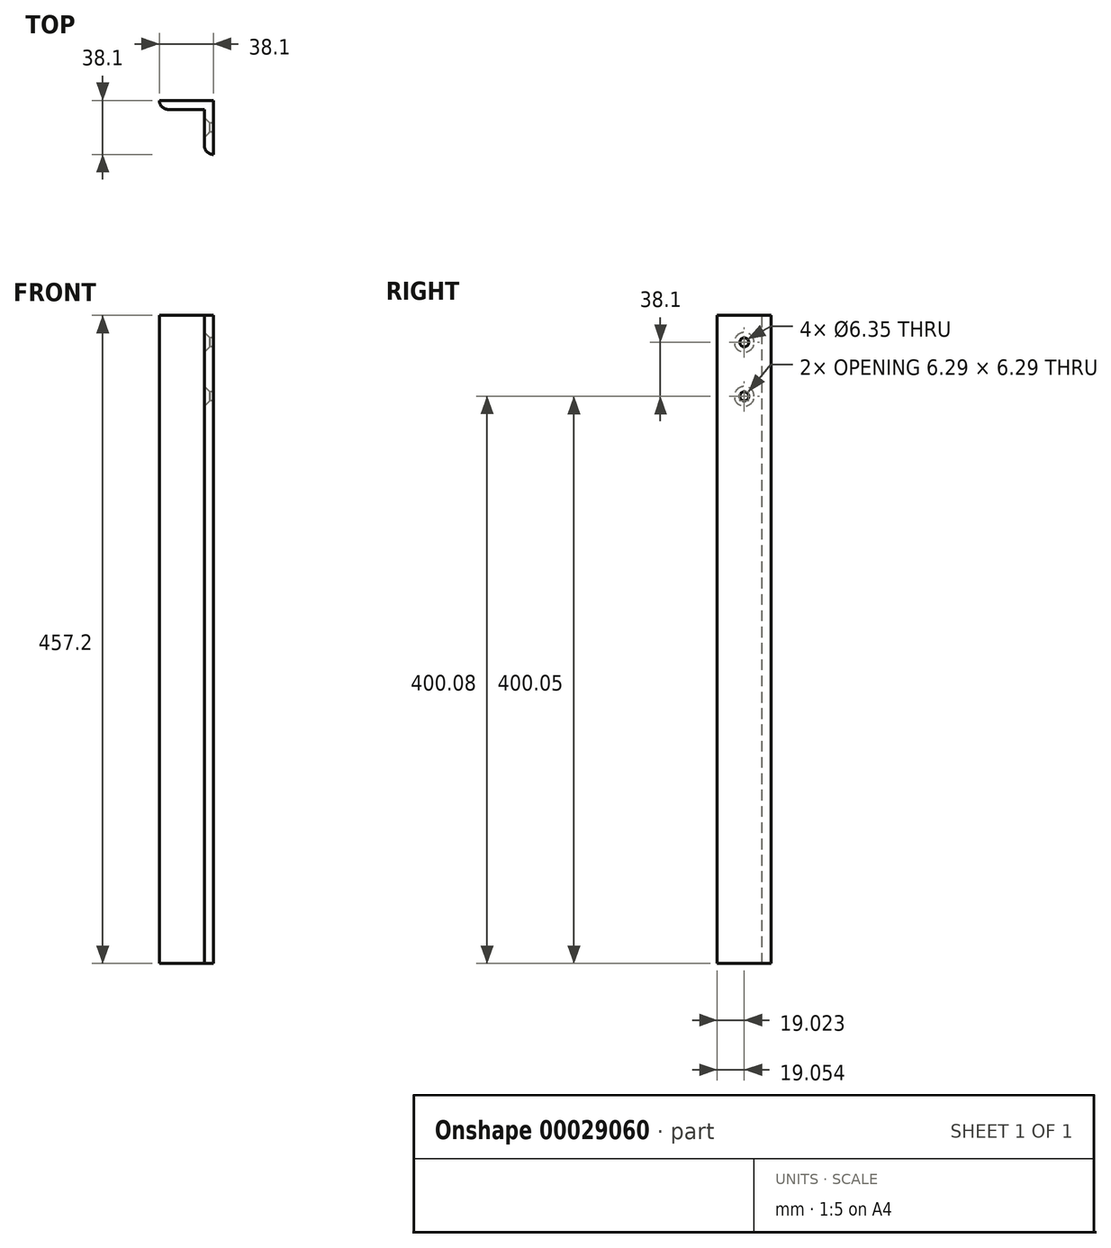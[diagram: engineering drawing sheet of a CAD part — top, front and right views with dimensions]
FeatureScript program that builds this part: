
annotation { "Feature Type Name" : "Feature", "Feature Type Description" : "" }
export const myFeature = defineFeature(function(context is Context, id is Id, definition is map)
    precondition{}
    {
        {
            var Q0;
            Q0=qCreatedBy(makeId("Top.planeOp"),FACE);
            var sketch = newSketch(context, id + "F0", { "sketchPlane" : qUnion([Q0])});
            skLineSegment(sketch, "E0.bottom", {"start": v(-21.42, 16.68) * mm, "end": v(16.68, 16.68) * mm});
            skLineSegment(sketch, "E0.top", {"start": v(-15.07, 10.33) * mm, "end": v(10.33, 10.33) * mm});
            skLineSegment(sketch, "E0.left", {"start": v(-21.42, 16.68) * mm, "end": v(-21.42, 16.68) * mm});
            skLineSegment(sketch, "E1.top", {"start": v(16.68, -21.42) * mm, "end": v(16.68, -21.42) * mm});
            skLineSegment(sketch, "E1.left", {"start": v(16.68, 16.68) * mm, "end": v(16.68, -21.42) * mm});
            skLineSegment(sketch, "E1.right", {"start": v(10.33, 10.33) * mm, "end": v(10.33, -15.07) * mm});
            skPoint(sketch, "E2.visualSharp", {"position": v(-21.42, 10.33) * mm});
            skArc(sketch, "E2.filletArc", {"start": v(-21.42, 16.68) * mm, "mid": v(-19.56, 12.2) * mm, "end": v(-15.07, 10.33) * mm});
            skPoint(sketch, "E3.visualSharp", {"position": v(10.33, -21.42) * mm});
            skArc(sketch, "E3.filletArc", {"start": v(10.33, -15.07) * mm, "mid": v(12.2, -19.56) * mm, "end": v(16.68, -21.42) * mm});
            skSolve(sketch);
        }
        {
            var Q0;
            Q0=makeQuery(id+"F0.imprint","IMPRINT",FACE,{"disambiguationData":[TD([[makeQuery(id+"F0.imprint","IMPRINT",EDGE,{"derivedFrom":sQuery(id+"F0.wireOp",EDGE,"E0.bottom")}),-1.0]])]});
            extrude(context, id + "F1", {"entities" : qUnion([Q0]), "oppositeDirection" : true, "depth" : 457.2 * mm});
        }
        {
            var Q0;
            Q0=makeQuery(id+"F1.opExtrude","SWEPT_FACE",FACE,{"disambiguationData":[OSD([sQuery(id+"F0.wireOp",EDGE,"E1.right")])]});
            var sketch = newSketch(context, id + "F2", { "sketchPlane" : qUnion([Q0])});
            skPoint(sketch, "E4", {"position": v(2.37, -19.05) * mm});
            skPoint(sketch, "E5", {"position": v(2.37, -57.15) * mm});
            skSolve(sketch);
        }
        {
            var Q0;
            Q0=sQuery(id+"F2.wireOp",VERTEX,"E4");
            var Q1;
            Q1=sQuery(id+"F2.wireOp",VERTEX,"E5");
            var Q2;
            Q2=makeQuery(id+"F1.opExtrude","SWEPT_BODY",BODY,{"disambiguationData":[OSD([sQuery(id+"F0.wireOp",EDGE,"E0.bottom"),sQuery(id+"F0.wireOp",EDGE,"E0.top"),sQuery(id+"F0.wireOp",EDGE,"E1.left"),sQuery(id+"F0.wireOp",EDGE,"E1.right"),sQuery(id+"F0.wireOp",EDGE,"E2.filletArc"),sQuery(id+"F0.wireOp",EDGE,"E3.filletArc")])]});
            hole(context, id + "F3", {"style" : HoleStyle.C_SINK, "holeDiameter" : 6.35 * mm, "cSinkDiameter" : 13.97 * mm, "endStyle" : HoleEndStyle.THROUGH, "locations" : qUnion([Q0, Q1]), "scope" : qUnion([Q2]), "cSinkAngle" : 90 * degree});
        }
    });
